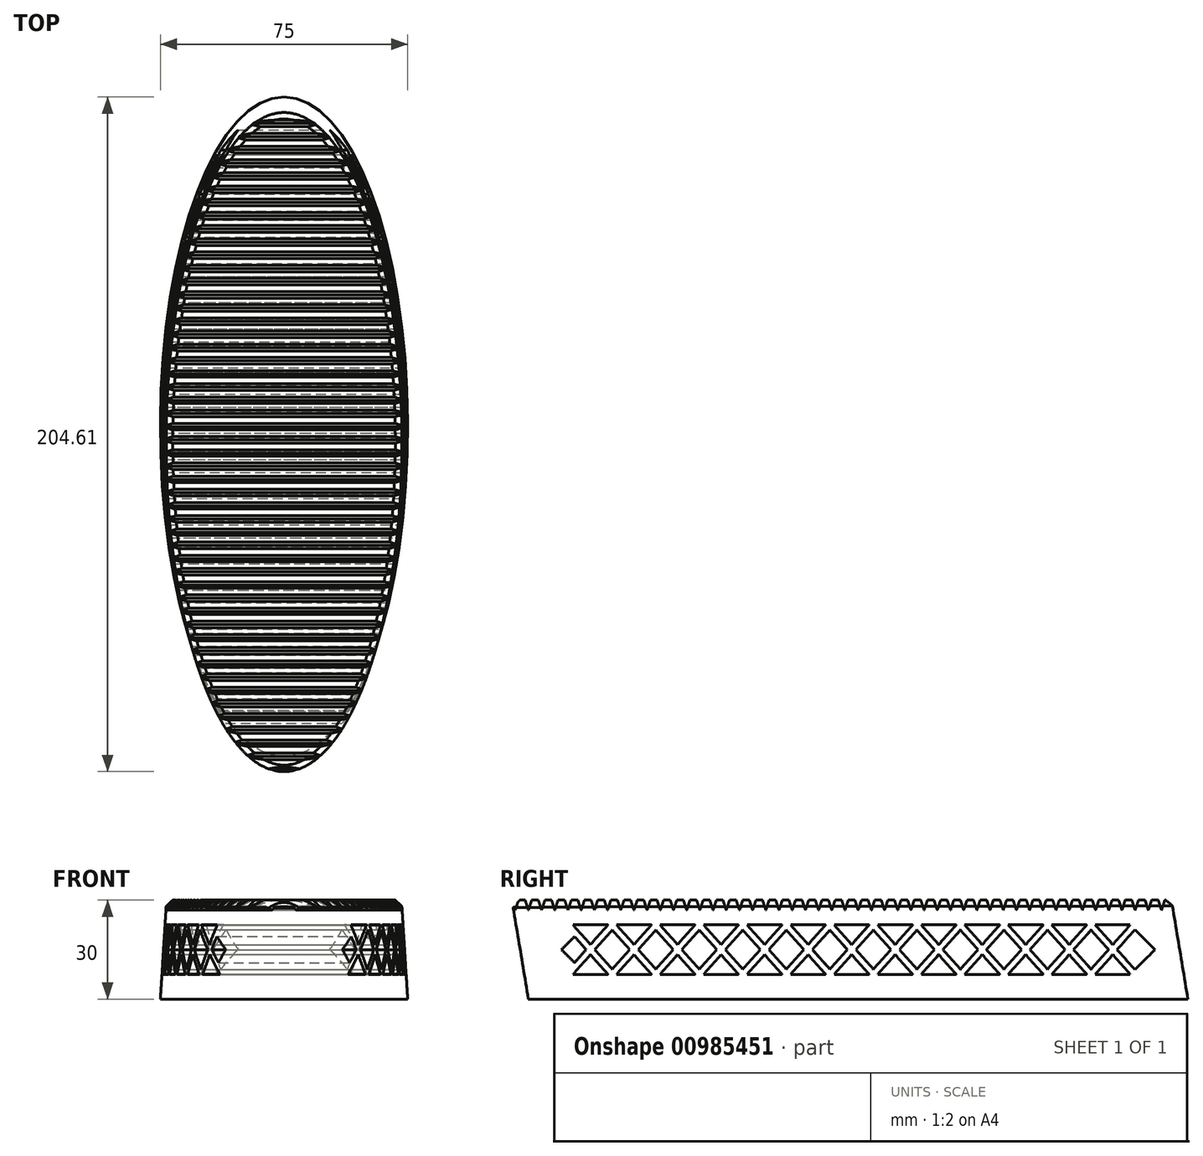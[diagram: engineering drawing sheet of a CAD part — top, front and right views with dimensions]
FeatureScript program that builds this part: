
annotation { "Feature Type Name" : "Feature", "Feature Type Description" : "" }
export const myFeature = defineFeature(function(context is Context, id is Id, definition is map)
    precondition{}
    {
        {
            assignVariable(context, id + "F0", {"name" : "Width", "anyValue" : 75});
        }
        {
            assignVariable(context, id + "F1", {"name" : "Thickness", "anyValue" : 30});
        }
        {
            var Q0;
            Q0=qCreatedBy(makeId("Top.planeOp"),FACE);
            var sketch = newSketch(context, id + "F2", { "sketchPlane" : qUnion([Q0])});
            skEllipse(sketch, "E0", {"center": v(0, 0) * mm, "majorRadius": 100 * mm, "minorRadius": 37.5 * mm, "majorAxis": v(0, 1)});
            skSolve(sketch);
        }
        {
            var Q0;
            Q0=makeQuery(id+"F2.imprint","IMPRINT",FACE,{"disambiguationData":[TD([[makeQuery(id+"F2.imprint","IMPRINT",EDGE,{"derivedFrom":sQuery(id+"F2.wireOp",EDGE,"E0")}),1.0]])]});
            cPlane(context, id + "F3", {"entities" : qUnion([Q0]), "cplaneType" : CPlaneType.OFFSET, "offset" : (getVariable(context, 'Thickness')) * mm, "width" : 150 * mm, "height" : 150 * mm});
        }
        {
            var Q0;
            Q0=qCreatedBy(id+"F3.planeOp",FACE);
            var sketch = newSketch(context, id + "F4", { "sketchPlane" : qUnion([Q0])});
            skEllipse(sketch, "E1", {"center": v(0, -5) * mm, "majorRadius": 100 * mm, "minorRadius": 35.63 * mm, "majorAxis": v(0, 1)});
            skEllipse(sketch, "E2.0", {"center": v(0, 0) * mm, "majorRadius": 100 * mm, "minorRadius": 37.5 * mm, "majorAxis": v(0, 1), "construction": true});
            skSolve(sketch);
        }
        {
            var Q0;
            Q0=makeQuery(id+"F2.imprint","IMPRINT",FACE,{"disambiguationData":[TD([[makeQuery(id+"F2.imprint","IMPRINT",EDGE,{"derivedFrom":sQuery(id+"F2.wireOp",EDGE,"E0")}),1.0]])]});
            var Q1;
            Q1=makeQuery(id+"F4.imprint","IMPRINT",FACE,{"disambiguationData":[TD([[makeQuery(id+"F4.imprint","IMPRINT",EDGE,{"derivedFrom":sQuery(id+"F4.wireOp",EDGE,"E1")}),1.0]])]});
            loft(context, id + "F5", {"sheetProfilesArray" : [{ "sheetProfileEntities" : qUnion([Q0]) }, { "sheetProfileEntities" : qUnion([Q1]) }]});
        }
        {
            var Q0;
            Q0=qCreatedBy(makeId("Right.planeOp"),FACE);
            var sketch = newSketch(context, id + "F6", { "sketchPlane" : qUnion([Q0])});
            skFitSpline(sketch, "E3.0", {"points": [v(95, 30) * mm, v(28.33, 30) * mm, v(-38.33, 30) * mm, v(-105, 30) * mm], "construction": true});
            skLineSegment(sketch, "E4", {"start": v(95, 30) * mm, "end": v(94, 33) * mm});
            skLineSegment(sketch, "E5", {"start": v(94, 33) * mm, "end": v(92, 27) * mm});
            skLineSegment(sketch, "E6", {"start": v(92, 27) * mm, "end": v(91, 30) * mm});
            skPoint(sketch, "E7", {"position": v(93, 30) * mm});
            skPoint(sketch, "E8", {"position": v(94, 30) * mm});
            skLineSegment(sketch, "E9.1.0.0", {"start": v(91, 30) * mm, "end": v(90, 33) * mm});
            skLineSegment(sketch, "E9.1.0.1", {"start": v(90, 33) * mm, "end": v(88, 27) * mm});
            skLineSegment(sketch, "E9.1.0.2", {"start": v(88, 27) * mm, "end": v(87, 30) * mm});
            skLineSegment(sketch, "E9.2.0.0", {"start": v(87, 30) * mm, "end": v(86, 33) * mm});
            skLineSegment(sketch, "E9.2.0.1", {"start": v(86, 33) * mm, "end": v(84, 27) * mm});
            skLineSegment(sketch, "E9.2.0.2", {"start": v(84, 27) * mm, "end": v(83, 30) * mm});
            skLineSegment(sketch, "E9.3.0.0", {"start": v(83, 30) * mm, "end": v(82, 33) * mm});
            skLineSegment(sketch, "E9.3.0.1", {"start": v(82, 33) * mm, "end": v(80, 27) * mm});
            skLineSegment(sketch, "E9.3.0.2", {"start": v(80, 27) * mm, "end": v(79, 30) * mm});
            skLineSegment(sketch, "E9.4.0.0", {"start": v(79, 30) * mm, "end": v(78, 33) * mm});
            skLineSegment(sketch, "E9.4.0.1", {"start": v(78, 33) * mm, "end": v(76, 27) * mm});
            skLineSegment(sketch, "E9.4.0.2", {"start": v(76, 27) * mm, "end": v(75, 30) * mm});
            skLineSegment(sketch, "E9.5.0.0", {"start": v(75, 30) * mm, "end": v(74, 33) * mm});
            skLineSegment(sketch, "E9.5.0.1", {"start": v(74, 33) * mm, "end": v(72, 27) * mm});
            skLineSegment(sketch, "E9.5.0.2", {"start": v(72, 27) * mm, "end": v(71, 30) * mm});
            skLineSegment(sketch, "E9.6.0.0", {"start": v(71, 30) * mm, "end": v(70, 33) * mm});
            skLineSegment(sketch, "E9.6.0.1", {"start": v(70, 33) * mm, "end": v(68, 27) * mm});
            skLineSegment(sketch, "E9.6.0.2", {"start": v(68, 27) * mm, "end": v(67, 30) * mm});
            skLineSegment(sketch, "E9.7.0.0", {"start": v(67, 30) * mm, "end": v(66, 33) * mm});
            skLineSegment(sketch, "E9.7.0.1", {"start": v(66, 33) * mm, "end": v(64, 27) * mm});
            skLineSegment(sketch, "E9.7.0.2", {"start": v(64, 27) * mm, "end": v(63, 30) * mm});
            skLineSegment(sketch, "E9.8.0.0", {"start": v(63, 30) * mm, "end": v(62, 33) * mm});
            skLineSegment(sketch, "E9.8.0.1", {"start": v(62, 33) * mm, "end": v(60, 27) * mm});
            skLineSegment(sketch, "E9.8.0.2", {"start": v(60, 27) * mm, "end": v(59, 30) * mm});
            skLineSegment(sketch, "E9.9.0.0", {"start": v(59, 30) * mm, "end": v(58, 33) * mm});
            skLineSegment(sketch, "E9.9.0.1", {"start": v(58, 33) * mm, "end": v(56, 27) * mm});
            skLineSegment(sketch, "E9.9.0.2", {"start": v(56, 27) * mm, "end": v(55, 30) * mm});
            skLineSegment(sketch, "E9.10.0.0", {"start": v(55, 30) * mm, "end": v(54, 33) * mm});
            skLineSegment(sketch, "E9.10.0.1", {"start": v(54, 33) * mm, "end": v(52, 27) * mm});
            skLineSegment(sketch, "E9.10.0.2", {"start": v(52, 27) * mm, "end": v(51, 30) * mm});
            skLineSegment(sketch, "E9.11.0.0", {"start": v(51, 30) * mm, "end": v(50, 33) * mm});
            skLineSegment(sketch, "E9.11.0.1", {"start": v(50, 33) * mm, "end": v(48, 27) * mm});
            skLineSegment(sketch, "E9.11.0.2", {"start": v(48, 27) * mm, "end": v(47, 30) * mm});
            skLineSegment(sketch, "E9.12.0.0", {"start": v(47, 30) * mm, "end": v(46, 33) * mm});
            skLineSegment(sketch, "E9.12.0.1", {"start": v(46, 33) * mm, "end": v(44, 27) * mm});
            skLineSegment(sketch, "E9.12.0.2", {"start": v(44, 27) * mm, "end": v(43, 30) * mm});
            skLineSegment(sketch, "E9.13.0.0", {"start": v(43, 30) * mm, "end": v(42, 33) * mm});
            skLineSegment(sketch, "E9.13.0.1", {"start": v(42, 33) * mm, "end": v(40, 27) * mm});
            skLineSegment(sketch, "E9.13.0.2", {"start": v(40, 27) * mm, "end": v(39, 30) * mm});
            skLineSegment(sketch, "E9.14.0.0", {"start": v(39, 30) * mm, "end": v(38, 33) * mm});
            skLineSegment(sketch, "E9.14.0.1", {"start": v(38, 33) * mm, "end": v(36, 27) * mm});
            skLineSegment(sketch, "E9.14.0.2", {"start": v(36, 27) * mm, "end": v(35, 30) * mm});
            skLineSegment(sketch, "E9.15.0.0", {"start": v(35, 30) * mm, "end": v(34, 33) * mm});
            skLineSegment(sketch, "E9.15.0.1", {"start": v(34, 33) * mm, "end": v(32, 27) * mm});
            skLineSegment(sketch, "E9.15.0.2", {"start": v(32, 27) * mm, "end": v(31, 30) * mm});
            skLineSegment(sketch, "E9.16.0.0", {"start": v(31, 30) * mm, "end": v(30, 33) * mm});
            skLineSegment(sketch, "E9.16.0.1", {"start": v(30, 33) * mm, "end": v(28, 27) * mm});
            skLineSegment(sketch, "E9.16.0.2", {"start": v(28, 27) * mm, "end": v(27, 30) * mm});
            skLineSegment(sketch, "E9.17.0.0", {"start": v(27, 30) * mm, "end": v(26, 33) * mm});
            skLineSegment(sketch, "E9.17.0.1", {"start": v(26, 33) * mm, "end": v(24, 27) * mm});
            skLineSegment(sketch, "E9.17.0.2", {"start": v(24, 27) * mm, "end": v(23, 30) * mm});
            skLineSegment(sketch, "E9.18.0.0", {"start": v(23, 30) * mm, "end": v(22, 33) * mm});
            skLineSegment(sketch, "E9.18.0.1", {"start": v(22, 33) * mm, "end": v(20, 27) * mm});
            skLineSegment(sketch, "E9.18.0.2", {"start": v(20, 27) * mm, "end": v(19, 30) * mm});
            skLineSegment(sketch, "E9.19.0.0", {"start": v(19, 30) * mm, "end": v(18, 33) * mm});
            skLineSegment(sketch, "E9.19.0.1", {"start": v(18, 33) * mm, "end": v(16, 27) * mm});
            skLineSegment(sketch, "E9.19.0.2", {"start": v(16, 27) * mm, "end": v(15, 30) * mm});
            skLineSegment(sketch, "E9.20.0.0", {"start": v(15, 30) * mm, "end": v(14, 33) * mm});
            skLineSegment(sketch, "E9.20.0.1", {"start": v(14, 33) * mm, "end": v(12, 27) * mm});
            skLineSegment(sketch, "E9.20.0.2", {"start": v(12, 27) * mm, "end": v(11, 30) * mm});
            skLineSegment(sketch, "E9.21.0.0", {"start": v(11, 30) * mm, "end": v(10, 33) * mm});
            skLineSegment(sketch, "E9.21.0.1", {"start": v(10, 33) * mm, "end": v(8, 27) * mm});
            skLineSegment(sketch, "E9.21.0.2", {"start": v(8, 27) * mm, "end": v(7, 30) * mm});
            skLineSegment(sketch, "E9.22.0.0", {"start": v(7, 30) * mm, "end": v(6, 33) * mm});
            skLineSegment(sketch, "E9.22.0.1", {"start": v(6, 33) * mm, "end": v(4, 27) * mm});
            skLineSegment(sketch, "E9.22.0.2", {"start": v(4, 27) * mm, "end": v(3, 30) * mm});
            skLineSegment(sketch, "E9.23.0.0", {"start": v(3, 30) * mm, "end": v(2, 33) * mm});
            skLineSegment(sketch, "E9.23.0.1", {"start": v(2, 33) * mm, "end": v(0, 27) * mm});
            skLineSegment(sketch, "E9.23.0.2", {"start": v(0, 27) * mm, "end": v(-1, 30) * mm});
            skLineSegment(sketch, "E9.24.0.0", {"start": v(-1, 30) * mm, "end": v(-2, 33) * mm});
            skLineSegment(sketch, "E9.24.0.1", {"start": v(-2, 33) * mm, "end": v(-4, 27) * mm});
            skLineSegment(sketch, "E9.24.0.2", {"start": v(-4, 27) * mm, "end": v(-5, 30) * mm});
            skLineSegment(sketch, "E9.25.0.0", {"start": v(-5, 30) * mm, "end": v(-6, 33) * mm});
            skLineSegment(sketch, "E9.25.0.1", {"start": v(-6, 33) * mm, "end": v(-8, 27) * mm});
            skLineSegment(sketch, "E9.25.0.2", {"start": v(-8, 27) * mm, "end": v(-9, 30) * mm});
            skLineSegment(sketch, "E9.26.0.0", {"start": v(-9, 30) * mm, "end": v(-10, 33) * mm});
            skLineSegment(sketch, "E9.26.0.1", {"start": v(-10, 33) * mm, "end": v(-12, 27) * mm});
            skLineSegment(sketch, "E9.26.0.2", {"start": v(-12, 27) * mm, "end": v(-13, 30) * mm});
            skLineSegment(sketch, "E9.27.0.0", {"start": v(-13, 30) * mm, "end": v(-14, 33) * mm});
            skLineSegment(sketch, "E9.27.0.1", {"start": v(-14, 33) * mm, "end": v(-16, 27) * mm});
            skLineSegment(sketch, "E9.27.0.2", {"start": v(-16, 27) * mm, "end": v(-17, 30) * mm});
            skLineSegment(sketch, "E9.28.0.0", {"start": v(-17, 30) * mm, "end": v(-18, 33) * mm});
            skLineSegment(sketch, "E9.28.0.1", {"start": v(-18, 33) * mm, "end": v(-20, 27) * mm});
            skLineSegment(sketch, "E9.28.0.2", {"start": v(-20, 27) * mm, "end": v(-21, 30) * mm});
            skLineSegment(sketch, "E9.29.0.0", {"start": v(-21, 30) * mm, "end": v(-22, 33) * mm});
            skLineSegment(sketch, "E9.29.0.1", {"start": v(-22, 33) * mm, "end": v(-24, 27) * mm});
            skLineSegment(sketch, "E9.29.0.2", {"start": v(-24, 27) * mm, "end": v(-25, 30) * mm});
            skLineSegment(sketch, "E9.30.0.0", {"start": v(-25, 30) * mm, "end": v(-26, 33) * mm});
            skLineSegment(sketch, "E9.30.0.1", {"start": v(-26, 33) * mm, "end": v(-28, 27) * mm});
            skLineSegment(sketch, "E9.30.0.2", {"start": v(-28, 27) * mm, "end": v(-29, 30) * mm});
            skLineSegment(sketch, "E9.31.0.0", {"start": v(-29, 30) * mm, "end": v(-30, 33) * mm});
            skLineSegment(sketch, "E9.31.0.1", {"start": v(-30, 33) * mm, "end": v(-32, 27) * mm});
            skLineSegment(sketch, "E9.31.0.2", {"start": v(-32, 27) * mm, "end": v(-33, 30) * mm});
            skLineSegment(sketch, "E9.32.0.0", {"start": v(-33, 30) * mm, "end": v(-34, 33) * mm});
            skLineSegment(sketch, "E9.32.0.1", {"start": v(-34, 33) * mm, "end": v(-36, 27) * mm});
            skLineSegment(sketch, "E9.32.0.2", {"start": v(-36, 27) * mm, "end": v(-37, 30) * mm});
            skLineSegment(sketch, "E9.33.0.0", {"start": v(-37, 30) * mm, "end": v(-38, 33) * mm});
            skLineSegment(sketch, "E9.33.0.1", {"start": v(-38, 33) * mm, "end": v(-40, 27) * mm});
            skLineSegment(sketch, "E9.33.0.2", {"start": v(-40, 27) * mm, "end": v(-41, 30) * mm});
            skLineSegment(sketch, "E9.34.0.0", {"start": v(-41, 30) * mm, "end": v(-42, 33) * mm});
            skLineSegment(sketch, "E9.34.0.1", {"start": v(-42, 33) * mm, "end": v(-44, 27) * mm});
            skLineSegment(sketch, "E9.34.0.2", {"start": v(-44, 27) * mm, "end": v(-45, 30) * mm});
            skLineSegment(sketch, "E9.35.0.0", {"start": v(-45, 30) * mm, "end": v(-46, 33) * mm});
            skLineSegment(sketch, "E9.35.0.1", {"start": v(-46, 33) * mm, "end": v(-48, 27) * mm});
            skLineSegment(sketch, "E9.35.0.2", {"start": v(-48, 27) * mm, "end": v(-49, 30) * mm});
            skLineSegment(sketch, "E9.36.0.0", {"start": v(-49, 30) * mm, "end": v(-50, 33) * mm});
            skLineSegment(sketch, "E9.36.0.1", {"start": v(-50, 33) * mm, "end": v(-52, 27) * mm});
            skLineSegment(sketch, "E9.36.0.2", {"start": v(-52, 27) * mm, "end": v(-53, 30) * mm});
            skLineSegment(sketch, "E9.37.0.0", {"start": v(-53, 30) * mm, "end": v(-54, 33) * mm});
            skLineSegment(sketch, "E9.37.0.1", {"start": v(-54, 33) * mm, "end": v(-56, 27) * mm});
            skLineSegment(sketch, "E9.37.0.2", {"start": v(-56, 27) * mm, "end": v(-57, 30) * mm});
            skLineSegment(sketch, "E9.38.0.0", {"start": v(-57, 30) * mm, "end": v(-58, 33) * mm});
            skLineSegment(sketch, "E9.38.0.1", {"start": v(-58, 33) * mm, "end": v(-60, 27) * mm});
            skLineSegment(sketch, "E9.38.0.2", {"start": v(-60, 27) * mm, "end": v(-61, 30) * mm});
            skLineSegment(sketch, "E9.39.0.0", {"start": v(-61, 30) * mm, "end": v(-62, 33) * mm});
            skLineSegment(sketch, "E9.39.0.1", {"start": v(-62, 33) * mm, "end": v(-64, 27) * mm});
            skLineSegment(sketch, "E9.39.0.2", {"start": v(-64, 27) * mm, "end": v(-65, 30) * mm});
            skLineSegment(sketch, "E9.40.0.0", {"start": v(-65, 30) * mm, "end": v(-66, 33) * mm});
            skLineSegment(sketch, "E9.40.0.1", {"start": v(-66, 33) * mm, "end": v(-68, 27) * mm});
            skLineSegment(sketch, "E9.40.0.2", {"start": v(-68, 27) * mm, "end": v(-69, 30) * mm});
            skLineSegment(sketch, "E9.41.0.0", {"start": v(-69, 30) * mm, "end": v(-70, 33) * mm});
            skLineSegment(sketch, "E9.41.0.1", {"start": v(-70, 33) * mm, "end": v(-72, 27) * mm});
            skLineSegment(sketch, "E9.41.0.2", {"start": v(-72, 27) * mm, "end": v(-73, 30) * mm});
            skLineSegment(sketch, "E9.42.0.0", {"start": v(-73, 30) * mm, "end": v(-74, 33) * mm});
            skLineSegment(sketch, "E9.42.0.1", {"start": v(-74, 33) * mm, "end": v(-76, 27) * mm});
            skLineSegment(sketch, "E9.42.0.2", {"start": v(-76, 27) * mm, "end": v(-77, 30) * mm});
            skLineSegment(sketch, "E9.43.0.0", {"start": v(-77, 30) * mm, "end": v(-78, 33) * mm});
            skLineSegment(sketch, "E9.43.0.1", {"start": v(-78, 33) * mm, "end": v(-80, 27) * mm});
            skLineSegment(sketch, "E9.43.0.2", {"start": v(-80, 27) * mm, "end": v(-81, 30) * mm});
            skLineSegment(sketch, "E9.44.0.0", {"start": v(-81, 30) * mm, "end": v(-82, 33) * mm});
            skLineSegment(sketch, "E9.44.0.1", {"start": v(-82, 33) * mm, "end": v(-84, 27) * mm});
            skLineSegment(sketch, "E9.44.0.2", {"start": v(-84, 27) * mm, "end": v(-85, 30) * mm});
            skLineSegment(sketch, "E9.45.0.0", {"start": v(-85, 30) * mm, "end": v(-86, 33) * mm});
            skLineSegment(sketch, "E9.45.0.1", {"start": v(-86, 33) * mm, "end": v(-88, 27) * mm});
            skLineSegment(sketch, "E9.45.0.2", {"start": v(-88, 27) * mm, "end": v(-89, 30) * mm});
            skLineSegment(sketch, "E9.46.0.0", {"start": v(-89, 30) * mm, "end": v(-90, 33) * mm});
            skLineSegment(sketch, "E9.46.0.1", {"start": v(-90, 33) * mm, "end": v(-92, 27) * mm});
            skLineSegment(sketch, "E9.46.0.2", {"start": v(-92, 27) * mm, "end": v(-93, 30) * mm});
            skLineSegment(sketch, "E9.47.0.0", {"start": v(-93, 30) * mm, "end": v(-94, 33) * mm});
            skLineSegment(sketch, "E9.47.0.1", {"start": v(-94, 33) * mm, "end": v(-96, 27) * mm});
            skLineSegment(sketch, "E9.47.0.2", {"start": v(-96, 27) * mm, "end": v(-97, 30) * mm});
            skLineSegment(sketch, "E9.48.0.0", {"start": v(-97, 30) * mm, "end": v(-98, 33) * mm});
            skLineSegment(sketch, "E9.48.0.1", {"start": v(-98, 33) * mm, "end": v(-100, 27) * mm});
            skLineSegment(sketch, "E9.48.0.2", {"start": v(-100, 27) * mm, "end": v(-101, 30) * mm});
            skLineSegment(sketch, "E9.49.0.0", {"start": v(-101, 30) * mm, "end": v(-102, 33) * mm});
            skLineSegment(sketch, "E9.49.0.1", {"start": v(-102, 33) * mm, "end": v(-104, 27) * mm});
            skLineSegment(sketch, "E9.49.0.2", {"start": v(-104, 27) * mm, "end": v(-105, 30) * mm});
            skLineSegment(sketch, "E9.direction1", {"start": v(95, 30) * mm, "end": v(91, 30) * mm, "construction": true});
            skLineSegment(sketch, "E10", {"start": v(94, 33) * mm, "end": v(-105, 33) * mm});
            skLineSegment(sketch, "E11", {"start": v(-105, 33) * mm, "end": v(-105, 30) * mm});
            skSolve(sketch);
        }
        {
            var Q0;
            Q0=makeQuery(id+"F5.opLoft","MID_CAP_EDGE",EDGE,{"disambiguationData":[OSD([sQuery(id+"F4.wireOp",EDGE,"E1")])],"capPos":1.0});
            chamfer(context, id + "F7", {"entities" : qUnion([Q0]), "width" : 2 * mm, "tangentPropagation" : true});
        }
        {
            var Q0;
            Q0 = qSketchRegion(id + "F6", true);
            extrude(context, id + "F8", {"entities" : qUnion([Q0]), "operationType" : NewBodyOperationType.REMOVE, "endBound" : BoundingType.SYMMETRIC, "oppositeDirection" : true, "depth" : (getVariable(context, 'Width')) * mm, "offsetDistance" : 25 * mm});
        }
        {
            var Q0;
            Q0=qCreatedBy(makeId("Right.planeOp"),FACE);
            var sketch = newSketch(context, id + "F9", { "sketchPlane" : qUnion([Q0])});
            skLineSegment(sketch, "E12.bottom", {"start": v(-90, 22.5) * mm, "end": v(90, 22.5) * mm});
            skLineSegment(sketch, "E12.top", {"start": v(-90, 7.5) * mm, "end": v(90, 7.5) * mm});
            skLineSegment(sketch, "E12.left", {"start": v(-90, 22.5) * mm, "end": v(-90, 7.5) * mm});
            skLineSegment(sketch, "E12.right", {"start": v(90, 22.5) * mm, "end": v(90, 7.5) * mm});
            skPoint(sketch, "E12.middle", {"position": v(0, 15) * mm});
            skLineSegment(sketch, "E13", {"start": v(90, 15) * mm, "end": v(82.5, 22.5) * mm});
            skLineSegment(sketch, "E14.MirrorCS", {"start": v(-90, 15) * mm, "end": v(-82.5, 22.5) * mm});
            skLineSegment(sketch, "E15", {"start": v(90, 15) * mm, "end": v(-90, 15) * mm, "construction": true});
            skLineSegment(sketch, "E16.MirrorCS", {"start": v(90, 15) * mm, "end": v(82.5, 7.5) * mm});
            skLineSegment(sketch, "E17.MirrorCS", {"start": v(-90, 15) * mm, "end": v(-82.5, 7.5) * mm});
            skLineSegment(sketch, "E18", {"start": v(82.5, 22.5) * mm, "end": v(69.27, 7.5) * mm});
            skLineSegment(sketch, "E19", {"start": v(83.92, 21.08) * mm, "end": v(71.94, 7.5) * mm});
            skLineSegment(sketch, "E20.MirrorCS", {"start": v(83.92, 8.92) * mm, "end": v(71.94, 22.5) * mm});
            skLineSegment(sketch, "E21.MirrorCS", {"start": v(82.5, 7.5) * mm, "end": v(69.27, 22.5) * mm});
            skLineSegment(sketch, "E22.1.0.0", {"start": v(70.72, 21.08) * mm, "end": v(58.74, 7.5) * mm});
            skLineSegment(sketch, "E22.1.0.1", {"start": v(69.3, 22.5) * mm, "end": v(56.07, 7.5) * mm});
            skLineSegment(sketch, "E22.1.0.2", {"start": v(70.72, 8.92) * mm, "end": v(58.74, 22.5) * mm});
            skLineSegment(sketch, "E22.1.0.3", {"start": v(69.3, 7.5) * mm, "end": v(56.07, 22.5) * mm});
            skLineSegment(sketch, "E22.1.0.4", {"start": v(76.8, 15) * mm, "end": v(-103.2, 15) * mm, "construction": true});
            skLineSegment(sketch, "E22.2.0.0", {"start": v(57.52, 21.08) * mm, "end": v(45.54, 7.5) * mm});
            skLineSegment(sketch, "E22.2.0.1", {"start": v(56.1, 22.5) * mm, "end": v(42.87, 7.5) * mm});
            skLineSegment(sketch, "E22.2.0.2", {"start": v(57.52, 8.92) * mm, "end": v(45.54, 22.5) * mm});
            skLineSegment(sketch, "E22.2.0.3", {"start": v(56.1, 7.5) * mm, "end": v(42.87, 22.5) * mm});
            skLineSegment(sketch, "E22.2.0.4", {"start": v(63.6, 15) * mm, "end": v(-116.4, 15) * mm, "construction": true});
            skLineSegment(sketch, "E22.3.0.0", {"start": v(44.32, 21.08) * mm, "end": v(32.34, 7.5) * mm});
            skLineSegment(sketch, "E22.3.0.1", {"start": v(42.9, 22.5) * mm, "end": v(29.67, 7.5) * mm});
            skLineSegment(sketch, "E22.3.0.2", {"start": v(44.32, 8.92) * mm, "end": v(32.34, 22.5) * mm});
            skLineSegment(sketch, "E22.3.0.3", {"start": v(42.9, 7.5) * mm, "end": v(29.67, 22.5) * mm});
            skLineSegment(sketch, "E22.3.0.4", {"start": v(50.4, 15) * mm, "end": v(-129.6, 15) * mm, "construction": true});
            skLineSegment(sketch, "E22.4.0.0", {"start": v(31.12, 21.08) * mm, "end": v(19.14, 7.5) * mm});
            skLineSegment(sketch, "E22.4.0.1", {"start": v(29.7, 22.5) * mm, "end": v(16.47, 7.5) * mm});
            skLineSegment(sketch, "E22.4.0.2", {"start": v(31.12, 8.92) * mm, "end": v(19.14, 22.5) * mm});
            skLineSegment(sketch, "E22.4.0.3", {"start": v(29.7, 7.5) * mm, "end": v(16.47, 22.5) * mm});
            skLineSegment(sketch, "E22.4.0.4", {"start": v(37.2, 15) * mm, "end": v(-142.8, 15) * mm, "construction": true});
            skLineSegment(sketch, "E22.5.0.0", {"start": v(17.92, 21.08) * mm, "end": v(5.94, 7.5) * mm});
            skLineSegment(sketch, "E22.5.0.1", {"start": v(16.5, 22.5) * mm, "end": v(3.27, 7.5) * mm});
            skLineSegment(sketch, "E22.5.0.2", {"start": v(17.92, 8.92) * mm, "end": v(5.94, 22.5) * mm});
            skLineSegment(sketch, "E22.5.0.3", {"start": v(16.5, 7.5) * mm, "end": v(3.27, 22.5) * mm});
            skLineSegment(sketch, "E22.5.0.4", {"start": v(24, 15) * mm, "end": v(-156, 15) * mm, "construction": true});
            skLineSegment(sketch, "E22.6.0.0", {"start": v(4.72, 21.08) * mm, "end": v(-7.26, 7.5) * mm});
            skLineSegment(sketch, "E22.6.0.1", {"start": v(3.3, 22.5) * mm, "end": v(-9.93, 7.5) * mm});
            skLineSegment(sketch, "E22.6.0.2", {"start": v(4.72, 8.92) * mm, "end": v(-7.26, 22.5) * mm});
            skLineSegment(sketch, "E22.6.0.3", {"start": v(3.3, 7.5) * mm, "end": v(-9.93, 22.5) * mm});
            skLineSegment(sketch, "E22.6.0.4", {"start": v(10.8, 15) * mm, "end": v(-169.2, 15) * mm, "construction": true});
            skLineSegment(sketch, "E22.7.0.0", {"start": v(-8.48, 21.08) * mm, "end": v(-20.46, 7.5) * mm});
            skLineSegment(sketch, "E22.7.0.1", {"start": v(-9.9, 22.5) * mm, "end": v(-23.13, 7.5) * mm});
            skLineSegment(sketch, "E22.7.0.2", {"start": v(-8.48, 8.92) * mm, "end": v(-20.46, 22.5) * mm});
            skLineSegment(sketch, "E22.7.0.3", {"start": v(-9.9, 7.5) * mm, "end": v(-23.13, 22.5) * mm});
            skLineSegment(sketch, "E22.7.0.4", {"start": v(-2.4, 15) * mm, "end": v(-182.4, 15) * mm, "construction": true});
            skLineSegment(sketch, "E22.8.0.0", {"start": v(-21.68, 21.08) * mm, "end": v(-33.66, 7.5) * mm});
            skLineSegment(sketch, "E22.8.0.1", {"start": v(-23.1, 22.5) * mm, "end": v(-36.33, 7.5) * mm});
            skLineSegment(sketch, "E22.8.0.2", {"start": v(-21.68, 8.92) * mm, "end": v(-33.66, 22.5) * mm});
            skLineSegment(sketch, "E22.8.0.3", {"start": v(-23.1, 7.5) * mm, "end": v(-36.33, 22.5) * mm});
            skLineSegment(sketch, "E22.8.0.4", {"start": v(-15.6, 15) * mm, "end": v(-195.6, 15) * mm, "construction": true});
            skLineSegment(sketch, "E22.9.0.0", {"start": v(-34.88, 21.08) * mm, "end": v(-46.86, 7.5) * mm});
            skLineSegment(sketch, "E22.9.0.1", {"start": v(-36.3, 22.5) * mm, "end": v(-49.53, 7.5) * mm});
            skLineSegment(sketch, "E22.9.0.2", {"start": v(-34.88, 8.92) * mm, "end": v(-46.86, 22.5) * mm});
            skLineSegment(sketch, "E22.9.0.3", {"start": v(-36.3, 7.5) * mm, "end": v(-49.53, 22.5) * mm});
            skLineSegment(sketch, "E22.9.0.4", {"start": v(-28.8, 15) * mm, "end": v(-208.8, 15) * mm, "construction": true});
            skLineSegment(sketch, "E22.10.0.0", {"start": v(-48.08, 21.08) * mm, "end": v(-60.06, 7.5) * mm});
            skLineSegment(sketch, "E22.10.0.1", {"start": v(-49.5, 22.5) * mm, "end": v(-62.73, 7.5) * mm});
            skLineSegment(sketch, "E22.10.0.2", {"start": v(-48.08, 8.92) * mm, "end": v(-60.06, 22.5) * mm});
            skLineSegment(sketch, "E22.10.0.3", {"start": v(-49.5, 7.5) * mm, "end": v(-62.73, 22.5) * mm});
            skLineSegment(sketch, "E22.10.0.4", {"start": v(-42, 15) * mm, "end": v(-222, 15) * mm, "construction": true});
            skLineSegment(sketch, "E22.11.0.0", {"start": v(-61.28, 21.08) * mm, "end": v(-73.26, 7.5) * mm});
            skLineSegment(sketch, "E22.11.0.1", {"start": v(-62.7, 22.5) * mm, "end": v(-75.93, 7.5) * mm});
            skLineSegment(sketch, "E22.11.0.2", {"start": v(-61.28, 8.92) * mm, "end": v(-73.26, 22.5) * mm});
            skLineSegment(sketch, "E22.11.0.3", {"start": v(-62.7, 7.5) * mm, "end": v(-75.93, 22.5) * mm});
            skLineSegment(sketch, "E22.11.0.4", {"start": v(-55.2, 15) * mm, "end": v(-235.2, 15) * mm, "construction": true});
            skLineSegment(sketch, "E22.12.0.0", {"start": v(-74.48, 21.08) * mm, "end": v(-86.46, 7.5) * mm});
            skLineSegment(sketch, "E22.12.0.1", {"start": v(-75.9, 22.5) * mm, "end": v(-89.13, 7.5) * mm});
            skLineSegment(sketch, "E22.12.0.2", {"start": v(-74.48, 8.92) * mm, "end": v(-86.46, 22.5) * mm});
            skLineSegment(sketch, "E22.12.0.3", {"start": v(-75.9, 7.5) * mm, "end": v(-89.13, 22.5) * mm});
            skLineSegment(sketch, "E22.12.0.4", {"start": v(-68.4, 15) * mm, "end": v(-248.4, 15) * mm, "construction": true});
            skLineSegment(sketch, "E22.direction1", {"start": v(71.94, 7.5) * mm, "end": v(58.74, 7.5) * mm, "construction": true});
            skSolve(sketch);
        }
        {
            var Q0;
            {var subQ0=sQuery(id+"F9.wireOp",EDGE,"E22.1.0.2");var subQ1=sQuery(id+"F9.wireOp",EDGE,"E18");var subQ2=makeQuery(id+"F9.imprint","INTERSECT",VERTEX,{"derivedFrom":[subQ1,subQ0]});Q0=makeQuery(id+"F9.imprint","IMPRINT",FACE,{"disambiguationData":[TD([[makeQuery(id+"F9.imprint","IMPRINT",EDGE,{"disambiguationData":[TD([[subQ2,1.0]])],"derivedFrom":subQ1}),-1.0]])]});}
            var Q1;
            {var subQ0=sQuery(id+"F9.wireOp",EDGE,"E22.2.0.2");var subQ1=sQuery(id+"F9.wireOp",EDGE,"E22.1.0.1");var subQ2=makeQuery(id+"F9.imprint","INTERSECT",VERTEX,{"derivedFrom":[subQ1,subQ0]});Q1=makeQuery(id+"F9.imprint","IMPRINT",FACE,{"disambiguationData":[TD([[makeQuery(id+"F9.imprint","IMPRINT",EDGE,{"disambiguationData":[TD([[subQ2,1.0]])],"derivedFrom":subQ1}),-1.0]])]});}
            var Q2;
            {var subQ0=sQuery(id+"F9.wireOp",EDGE,"E22.4.0.2");var subQ1=sQuery(id+"F9.wireOp",EDGE,"E22.3.0.1");var subQ2=makeQuery(id+"F9.imprint","INTERSECT",VERTEX,{"derivedFrom":[subQ1,subQ0]});Q2=makeQuery(id+"F9.imprint","IMPRINT",FACE,{"disambiguationData":[TD([[makeQuery(id+"F9.imprint","IMPRINT",EDGE,{"disambiguationData":[TD([[subQ2,1.0]])],"derivedFrom":subQ1}),-1.0]])]});}
            var Q3;
            {var subQ0=sQuery(id+"F9.wireOp",EDGE,"E22.5.0.2");var subQ1=sQuery(id+"F9.wireOp",EDGE,"E22.4.0.1");var subQ2=makeQuery(id+"F9.imprint","INTERSECT",VERTEX,{"derivedFrom":[subQ1,subQ0]});Q3=makeQuery(id+"F9.imprint","IMPRINT",FACE,{"disambiguationData":[TD([[makeQuery(id+"F9.imprint","IMPRINT",EDGE,{"disambiguationData":[TD([[subQ2,1.0]])],"derivedFrom":subQ1}),-1.0]])]});}
            var Q4;
            {var subQ0=sQuery(id+"F9.wireOp",EDGE,"E22.3.0.2");var subQ1=sQuery(id+"F9.wireOp",EDGE,"E22.2.0.1");var subQ2=makeQuery(id+"F9.imprint","INTERSECT",VERTEX,{"derivedFrom":[subQ1,subQ0]});Q4=makeQuery(id+"F9.imprint","IMPRINT",FACE,{"disambiguationData":[TD([[makeQuery(id+"F9.imprint","IMPRINT",EDGE,{"disambiguationData":[TD([[subQ2,1.0]])],"derivedFrom":subQ1}),-1.0]])]});}
            var Q5;
            {var subQ0=sQuery(id+"F9.wireOp",EDGE,"E22.6.0.2");var subQ1=sQuery(id+"F9.wireOp",EDGE,"E22.5.0.1");var subQ2=makeQuery(id+"F9.imprint","INTERSECT",VERTEX,{"derivedFrom":[subQ1,subQ0]});Q5=makeQuery(id+"F9.imprint","IMPRINT",FACE,{"disambiguationData":[TD([[makeQuery(id+"F9.imprint","IMPRINT",EDGE,{"disambiguationData":[TD([[subQ2,1.0]])],"derivedFrom":subQ1}),-1.0]])]});}
            var Q6;
            {var subQ0=sQuery(id+"F9.wireOp",EDGE,"E22.7.0.2");var subQ1=sQuery(id+"F9.wireOp",EDGE,"E22.6.0.1");var subQ2=makeQuery(id+"F9.imprint","INTERSECT",VERTEX,{"derivedFrom":[subQ1,subQ0]});Q6=makeQuery(id+"F9.imprint","IMPRINT",FACE,{"disambiguationData":[TD([[makeQuery(id+"F9.imprint","IMPRINT",EDGE,{"disambiguationData":[TD([[subQ2,1.0]])],"derivedFrom":subQ1}),-1.0]])]});}
            var Q7;
            {var subQ0=sQuery(id+"F9.wireOp",EDGE,"E22.8.0.2");var subQ1=sQuery(id+"F9.wireOp",EDGE,"E22.7.0.1");var subQ2=makeQuery(id+"F9.imprint","INTERSECT",VERTEX,{"derivedFrom":[subQ1,subQ0]});Q7=makeQuery(id+"F9.imprint","IMPRINT",FACE,{"disambiguationData":[TD([[makeQuery(id+"F9.imprint","IMPRINT",EDGE,{"disambiguationData":[TD([[subQ2,1.0]])],"derivedFrom":subQ1}),-1.0]])]});}
            var Q8;
            {var subQ0=sQuery(id+"F9.wireOp",EDGE,"E22.9.0.2");var subQ1=sQuery(id+"F9.wireOp",EDGE,"E22.8.0.1");var subQ2=makeQuery(id+"F9.imprint","INTERSECT",VERTEX,{"derivedFrom":[subQ1,subQ0]});Q8=makeQuery(id+"F9.imprint","IMPRINT",FACE,{"disambiguationData":[TD([[makeQuery(id+"F9.imprint","IMPRINT",EDGE,{"disambiguationData":[TD([[subQ2,1.0]])],"derivedFrom":subQ1}),-1.0]])]});}
            var Q9;
            {var subQ0=sQuery(id+"F9.wireOp",EDGE,"E22.10.0.2");var subQ1=sQuery(id+"F9.wireOp",EDGE,"E22.9.0.1");var subQ2=makeQuery(id+"F9.imprint","INTERSECT",VERTEX,{"derivedFrom":[subQ1,subQ0]});Q9=makeQuery(id+"F9.imprint","IMPRINT",FACE,{"disambiguationData":[TD([[makeQuery(id+"F9.imprint","IMPRINT",EDGE,{"disambiguationData":[TD([[subQ2,1.0]])],"derivedFrom":subQ1}),-1.0]])]});}
            var Q10;
            {var subQ0=sQuery(id+"F9.wireOp",EDGE,"E22.11.0.2");var subQ1=sQuery(id+"F9.wireOp",EDGE,"E22.10.0.1");var subQ2=makeQuery(id+"F9.imprint","INTERSECT",VERTEX,{"derivedFrom":[subQ1,subQ0]});Q10=makeQuery(id+"F9.imprint","IMPRINT",FACE,{"disambiguationData":[TD([[makeQuery(id+"F9.imprint","IMPRINT",EDGE,{"disambiguationData":[TD([[subQ2,1.0]])],"derivedFrom":subQ1}),-1.0]])]});}
            var Q11;
            {var subQ0=sQuery(id+"F9.wireOp",EDGE,"E22.12.0.2");var subQ1=sQuery(id+"F9.wireOp",EDGE,"E22.11.0.1");var subQ2=makeQuery(id+"F9.imprint","INTERSECT",VERTEX,{"derivedFrom":[subQ1,subQ0]});Q11=makeQuery(id+"F9.imprint","IMPRINT",FACE,{"disambiguationData":[TD([[makeQuery(id+"F9.imprint","IMPRINT",EDGE,{"disambiguationData":[TD([[subQ2,1.0]])],"derivedFrom":subQ1}),-1.0]])]});}
            var Q12;
            {var subQ0=sQuery(id+"F9.wireOp",EDGE,"E17.MirrorCS");var subQ5=sQuery(id+"F9.wireOp",EDGE,"E22.12.0.1");var subQ6=makeQuery(id+"F9.imprint","INTERSECT",VERTEX,{"derivedFrom":[subQ0,subQ5]});Q12=makeQuery(id+"F9.imprint","IMPRINT",FACE,{"disambiguationData":[TD([[makeQuery(id+"F9.imprint","IMPRINT",EDGE,{"disambiguationData":[TD([[subQ6,1.0]])],"derivedFrom":subQ5}),-1.0]])]});}
            var Q13;
            {var subQ1=sQuery(id+"F9.wireOp",EDGE,"E17.MirrorCS");var subQ6=sQuery(id+"F9.wireOp",EDGE,"E12.top");var subQ9=makeQuery(id+"F9.imprint","INTERSECT",VERTEX,{"derivedFrom":[subQ6,subQ1]});Q13=makeQuery(id+"F9.imprint","IMPRINT",FACE,{"disambiguationData":[TD([[makeQuery(id+"F9.imprint","IMPRINT",EDGE,{"disambiguationData":[TD([[subQ9,-1.0]])],"derivedFrom":subQ6}),1.0]])]});}
            var Q14;
            {var subQ0=sQuery(id+"F9.wireOp",EDGE,"E17.MirrorCS");var subQ1=sQuery(id+"F9.wireOp",EDGE,"E12.top");var subQ2=makeQuery(id+"F9.imprint","INTERSECT",VERTEX,{"derivedFrom":[subQ1,subQ0]});Q14=makeQuery(id+"F9.imprint","IMPRINT",FACE,{"disambiguationData":[TD([[makeQuery(id+"F9.imprint","IMPRINT",EDGE,{"disambiguationData":[TD([[subQ2,1.0]])],"derivedFrom":subQ1}),1.0]])]});}
            var Q15;
            {var subQ1=sQuery(id+"F9.wireOp",EDGE,"E12.bottom");var subQ7=sQuery(id+"F9.wireOp",EDGE,"E14.MirrorCS");var subQ8=makeQuery(id+"F9.imprint","INTERSECT",VERTEX,{"derivedFrom":[subQ1,subQ7]});Q15=makeQuery(id+"F9.imprint","IMPRINT",FACE,{"disambiguationData":[TD([[makeQuery(id+"F9.imprint","IMPRINT",EDGE,{"disambiguationData":[TD([[subQ8,-1.0]])],"derivedFrom":subQ1}),-1.0]])]});}
            var Q16;
            {var subQ0=sQuery(id+"F9.wireOp",EDGE,"E14.MirrorCS");var subQ1=sQuery(id+"F9.wireOp",EDGE,"E12.bottom");var subQ2=makeQuery(id+"F9.imprint","INTERSECT",VERTEX,{"derivedFrom":[subQ1,subQ0]});Q16=makeQuery(id+"F9.imprint","IMPRINT",FACE,{"disambiguationData":[TD([[makeQuery(id+"F9.imprint","IMPRINT",EDGE,{"disambiguationData":[TD([[subQ2,1.0]])],"derivedFrom":subQ1}),-1.0]])]});}
            var Q17;
            {var subQ0=sQuery(id+"F9.wireOp",EDGE,"E22.10.0.3");var subQ1=sQuery(id+"F9.wireOp",EDGE,"E12.bottom");var subQ2=makeQuery(id+"F9.imprint","INTERSECT",VERTEX,{"derivedFrom":[subQ1,subQ0]});Q17=makeQuery(id+"F9.imprint","IMPRINT",FACE,{"disambiguationData":[TD([[makeQuery(id+"F9.imprint","IMPRINT",EDGE,{"disambiguationData":[TD([[subQ2,1.0]])],"derivedFrom":subQ1}),-1.0]])]});}
            var Q18;
            {var subQ0=sQuery(id+"F9.wireOp",EDGE,"E22.10.0.1");var subQ1=sQuery(id+"F9.wireOp",EDGE,"E12.top");var subQ2=makeQuery(id+"F9.imprint","INTERSECT",VERTEX,{"derivedFrom":[subQ1,subQ0]});Q18=makeQuery(id+"F9.imprint","IMPRINT",FACE,{"disambiguationData":[TD([[makeQuery(id+"F9.imprint","IMPRINT",EDGE,{"disambiguationData":[TD([[subQ2,1.0]])],"derivedFrom":subQ1}),1.0]])]});}
            var Q19;
            {var subQ0=sQuery(id+"F9.wireOp",EDGE,"E22.9.0.1");var subQ1=sQuery(id+"F9.wireOp",EDGE,"E12.top");var subQ2=makeQuery(id+"F9.imprint","INTERSECT",VERTEX,{"derivedFrom":[subQ1,subQ0]});Q19=makeQuery(id+"F9.imprint","IMPRINT",FACE,{"disambiguationData":[TD([[makeQuery(id+"F9.imprint","IMPRINT",EDGE,{"disambiguationData":[TD([[subQ2,1.0]])],"derivedFrom":subQ1}),1.0]])]});}
            var Q20;
            {var subQ0=sQuery(id+"F9.wireOp",EDGE,"E22.8.0.1");var subQ1=sQuery(id+"F9.wireOp",EDGE,"E12.top");var subQ2=makeQuery(id+"F9.imprint","INTERSECT",VERTEX,{"derivedFrom":[subQ1,subQ0]});Q20=makeQuery(id+"F9.imprint","IMPRINT",FACE,{"disambiguationData":[TD([[makeQuery(id+"F9.imprint","IMPRINT",EDGE,{"disambiguationData":[TD([[subQ2,1.0]])],"derivedFrom":subQ1}),1.0]])]});}
            var Q21;
            {var subQ0=sQuery(id+"F9.wireOp",EDGE,"E22.8.0.3");var subQ1=sQuery(id+"F9.wireOp",EDGE,"E12.bottom");var subQ2=makeQuery(id+"F9.imprint","INTERSECT",VERTEX,{"derivedFrom":[subQ1,subQ0]});Q21=makeQuery(id+"F9.imprint","IMPRINT",FACE,{"disambiguationData":[TD([[makeQuery(id+"F9.imprint","IMPRINT",EDGE,{"disambiguationData":[TD([[subQ2,1.0]])],"derivedFrom":subQ1}),-1.0]])]});}
            var Q22;
            {var subQ0=sQuery(id+"F9.wireOp",EDGE,"E22.7.0.3");var subQ1=sQuery(id+"F9.wireOp",EDGE,"E12.bottom");var subQ2=makeQuery(id+"F9.imprint","INTERSECT",VERTEX,{"derivedFrom":[subQ1,subQ0]});Q22=makeQuery(id+"F9.imprint","IMPRINT",FACE,{"disambiguationData":[TD([[makeQuery(id+"F9.imprint","IMPRINT",EDGE,{"disambiguationData":[TD([[subQ2,1.0]])],"derivedFrom":subQ1}),-1.0]])]});}
            var Q23;
            {var subQ0=sQuery(id+"F9.wireOp",EDGE,"E22.7.0.1");var subQ1=sQuery(id+"F9.wireOp",EDGE,"E12.top");var subQ2=makeQuery(id+"F9.imprint","INTERSECT",VERTEX,{"derivedFrom":[subQ1,subQ0]});Q23=makeQuery(id+"F9.imprint","IMPRINT",FACE,{"disambiguationData":[TD([[makeQuery(id+"F9.imprint","IMPRINT",EDGE,{"disambiguationData":[TD([[subQ2,1.0]])],"derivedFrom":subQ1}),1.0]])]});}
            var Q24;
            {var subQ0=sQuery(id+"F9.wireOp",EDGE,"E22.6.0.1");var subQ1=sQuery(id+"F9.wireOp",EDGE,"E12.top");var subQ2=makeQuery(id+"F9.imprint","INTERSECT",VERTEX,{"derivedFrom":[subQ1,subQ0]});Q24=makeQuery(id+"F9.imprint","IMPRINT",FACE,{"disambiguationData":[TD([[makeQuery(id+"F9.imprint","IMPRINT",EDGE,{"disambiguationData":[TD([[subQ2,1.0]])],"derivedFrom":subQ1}),1.0]])]});}
            var Q25;
            {var subQ0=sQuery(id+"F9.wireOp",EDGE,"E22.6.0.3");var subQ1=sQuery(id+"F9.wireOp",EDGE,"E12.bottom");var subQ2=makeQuery(id+"F9.imprint","INTERSECT",VERTEX,{"derivedFrom":[subQ1,subQ0]});Q25=makeQuery(id+"F9.imprint","IMPRINT",FACE,{"disambiguationData":[TD([[makeQuery(id+"F9.imprint","IMPRINT",EDGE,{"disambiguationData":[TD([[subQ2,1.0]])],"derivedFrom":subQ1}),-1.0]])]});}
            var Q26;
            {var subQ0=sQuery(id+"F9.wireOp",EDGE,"E22.5.0.3");var subQ1=sQuery(id+"F9.wireOp",EDGE,"E12.bottom");var subQ2=makeQuery(id+"F9.imprint","INTERSECT",VERTEX,{"derivedFrom":[subQ1,subQ0]});Q26=makeQuery(id+"F9.imprint","IMPRINT",FACE,{"disambiguationData":[TD([[makeQuery(id+"F9.imprint","IMPRINT",EDGE,{"disambiguationData":[TD([[subQ2,1.0]])],"derivedFrom":subQ1}),-1.0]])]});}
            var Q27;
            {var subQ0=sQuery(id+"F9.wireOp",EDGE,"E22.5.0.1");var subQ1=sQuery(id+"F9.wireOp",EDGE,"E12.top");var subQ2=makeQuery(id+"F9.imprint","INTERSECT",VERTEX,{"derivedFrom":[subQ1,subQ0]});Q27=makeQuery(id+"F9.imprint","IMPRINT",FACE,{"disambiguationData":[TD([[makeQuery(id+"F9.imprint","IMPRINT",EDGE,{"disambiguationData":[TD([[subQ2,1.0]])],"derivedFrom":subQ1}),1.0]])]});}
            var Q28;
            {var subQ0=sQuery(id+"F9.wireOp",EDGE,"E22.9.0.3");var subQ1=sQuery(id+"F9.wireOp",EDGE,"E12.bottom");var subQ2=makeQuery(id+"F9.imprint","INTERSECT",VERTEX,{"derivedFrom":[subQ1,subQ0]});Q28=makeQuery(id+"F9.imprint","IMPRINT",FACE,{"disambiguationData":[TD([[makeQuery(id+"F9.imprint","IMPRINT",EDGE,{"disambiguationData":[TD([[subQ2,1.0]])],"derivedFrom":subQ1}),-1.0]])]});}
            var Q29;
            {var subQ0=sQuery(id+"F9.wireOp",EDGE,"E22.4.0.3");var subQ1=sQuery(id+"F9.wireOp",EDGE,"E12.bottom");var subQ2=makeQuery(id+"F9.imprint","INTERSECT",VERTEX,{"derivedFrom":[subQ1,subQ0]});Q29=makeQuery(id+"F9.imprint","IMPRINT",FACE,{"disambiguationData":[TD([[makeQuery(id+"F9.imprint","IMPRINT",EDGE,{"disambiguationData":[TD([[subQ2,1.0]])],"derivedFrom":subQ1}),-1.0]])]});}
            var Q30;
            {var subQ0=sQuery(id+"F9.wireOp",EDGE,"E22.4.0.1");var subQ1=sQuery(id+"F9.wireOp",EDGE,"E12.top");var subQ2=makeQuery(id+"F9.imprint","INTERSECT",VERTEX,{"derivedFrom":[subQ1,subQ0]});Q30=makeQuery(id+"F9.imprint","IMPRINT",FACE,{"disambiguationData":[TD([[makeQuery(id+"F9.imprint","IMPRINT",EDGE,{"disambiguationData":[TD([[subQ2,1.0]])],"derivedFrom":subQ1}),1.0]])]});}
            var Q31;
            {var subQ0=sQuery(id+"F9.wireOp",EDGE,"E22.3.0.1");var subQ1=sQuery(id+"F9.wireOp",EDGE,"E12.top");var subQ2=makeQuery(id+"F9.imprint","INTERSECT",VERTEX,{"derivedFrom":[subQ1,subQ0]});Q31=makeQuery(id+"F9.imprint","IMPRINT",FACE,{"disambiguationData":[TD([[makeQuery(id+"F9.imprint","IMPRINT",EDGE,{"disambiguationData":[TD([[subQ2,1.0]])],"derivedFrom":subQ1}),1.0]])]});}
            var Q32;
            {var subQ0=sQuery(id+"F9.wireOp",EDGE,"E22.3.0.3");var subQ1=sQuery(id+"F9.wireOp",EDGE,"E12.bottom");var subQ2=makeQuery(id+"F9.imprint","INTERSECT",VERTEX,{"derivedFrom":[subQ1,subQ0]});Q32=makeQuery(id+"F9.imprint","IMPRINT",FACE,{"disambiguationData":[TD([[makeQuery(id+"F9.imprint","IMPRINT",EDGE,{"disambiguationData":[TD([[subQ2,1.0]])],"derivedFrom":subQ1}),-1.0]])]});}
            var Q33;
            {var subQ0=sQuery(id+"F9.wireOp",EDGE,"E22.2.0.3");var subQ1=sQuery(id+"F9.wireOp",EDGE,"E12.bottom");var subQ2=makeQuery(id+"F9.imprint","INTERSECT",VERTEX,{"derivedFrom":[subQ1,subQ0]});Q33=makeQuery(id+"F9.imprint","IMPRINT",FACE,{"disambiguationData":[TD([[makeQuery(id+"F9.imprint","IMPRINT",EDGE,{"disambiguationData":[TD([[subQ2,1.0]])],"derivedFrom":subQ1}),-1.0]])]});}
            var Q34;
            {var subQ0=sQuery(id+"F9.wireOp",EDGE,"E22.2.0.1");var subQ1=sQuery(id+"F9.wireOp",EDGE,"E12.top");var subQ2=makeQuery(id+"F9.imprint","INTERSECT",VERTEX,{"derivedFrom":[subQ1,subQ0]});Q34=makeQuery(id+"F9.imprint","IMPRINT",FACE,{"disambiguationData":[TD([[makeQuery(id+"F9.imprint","IMPRINT",EDGE,{"disambiguationData":[TD([[subQ2,1.0]])],"derivedFrom":subQ1}),1.0]])]});}
            var Q35;
            {var subQ0=sQuery(id+"F9.wireOp",EDGE,"E22.1.0.1");var subQ1=sQuery(id+"F9.wireOp",EDGE,"E12.top");var subQ2=makeQuery(id+"F9.imprint","INTERSECT",VERTEX,{"derivedFrom":[subQ1,subQ0]});Q35=makeQuery(id+"F9.imprint","IMPRINT",FACE,{"disambiguationData":[TD([[makeQuery(id+"F9.imprint","IMPRINT",EDGE,{"disambiguationData":[TD([[subQ2,1.0]])],"derivedFrom":subQ1}),1.0]])]});}
            var Q36;
            {var subQ0=sQuery(id+"F9.wireOp",EDGE,"E22.1.0.3");var subQ1=sQuery(id+"F9.wireOp",EDGE,"E12.bottom");var subQ2=makeQuery(id+"F9.imprint","INTERSECT",VERTEX,{"derivedFrom":[subQ1,subQ0]});Q36=makeQuery(id+"F9.imprint","IMPRINT",FACE,{"disambiguationData":[TD([[makeQuery(id+"F9.imprint","IMPRINT",EDGE,{"disambiguationData":[TD([[subQ2,1.0]])],"derivedFrom":subQ1}),-1.0]])]});}
            var Q37;
            {var subQ0=sQuery(id+"F9.wireOp",EDGE,"E21.MirrorCS");var subQ1=sQuery(id+"F9.wireOp",EDGE,"E12.bottom");var subQ2=makeQuery(id+"F9.imprint","INTERSECT",VERTEX,{"derivedFrom":[subQ1,subQ0]});Q37=makeQuery(id+"F9.imprint","IMPRINT",FACE,{"disambiguationData":[TD([[makeQuery(id+"F9.imprint","IMPRINT",EDGE,{"disambiguationData":[TD([[subQ2,1.0]])],"derivedFrom":subQ1}),-1.0]])]});}
            var Q38;
            {var subQ1=sQuery(id+"F9.wireOp",EDGE,"E12.top");var subQ3=sQuery(id+"F9.wireOp",EDGE,"E19");var subQ4=makeQuery(id+"F9.imprint","INTERSECT",VERTEX,{"derivedFrom":[subQ1,subQ3]});Q38=makeQuery(id+"F9.imprint","IMPRINT",FACE,{"disambiguationData":[TD([[makeQuery(id+"F9.imprint","IMPRINT",EDGE,{"disambiguationData":[TD([[subQ4,1.0]])],"derivedFrom":subQ3}),1.0]])]});}
            var Q39;
            {var subQ1=sQuery(id+"F9.wireOp",EDGE,"E12.bottom");var subQ3=sQuery(id+"F9.wireOp",EDGE,"E20.MirrorCS");var subQ4=makeQuery(id+"F9.imprint","INTERSECT",VERTEX,{"derivedFrom":[subQ1,subQ3]});Q39=makeQuery(id+"F9.imprint","IMPRINT",FACE,{"disambiguationData":[TD([[makeQuery(id+"F9.imprint","IMPRINT",EDGE,{"disambiguationData":[TD([[subQ4,1.0]])],"derivedFrom":subQ3}),-1.0]])]});}
            var Q40;
            {var subQ1=sQuery(id+"F9.wireOp",EDGE,"E13");var subQ3=sQuery(id+"F9.wireOp",EDGE,"E19");var subQ4=makeQuery(id+"F9.imprint","INTERSECT",VERTEX,{"derivedFrom":[subQ1,subQ3]});Q40=makeQuery(id+"F9.imprint","IMPRINT",FACE,{"disambiguationData":[TD([[makeQuery(id+"F9.imprint","IMPRINT",EDGE,{"disambiguationData":[TD([[subQ4,-1.0]])],"derivedFrom":subQ3}),1.0]])]});}
            var Q41;
            {var subQ0=sQuery(id+"F9.wireOp",EDGE,"E18");var subQ1=sQuery(id+"F9.wireOp",EDGE,"E12.top");var subQ2=makeQuery(id+"F9.imprint","INTERSECT",VERTEX,{"derivedFrom":[subQ1,subQ0]});Q41=makeQuery(id+"F9.imprint","IMPRINT",FACE,{"disambiguationData":[TD([[makeQuery(id+"F9.imprint","IMPRINT",EDGE,{"disambiguationData":[TD([[subQ2,1.0]])],"derivedFrom":subQ1}),1.0]])]});}
            extrude(context, id + "F10", {"entities" : qUnion([Q0, Q1, Q2, Q3, Q4, Q5, Q6, Q7, Q8, Q9, Q10, Q11, Q12, Q13, Q14, Q15, Q16, Q17, Q18, Q19, Q20, Q21, Q22, Q23, Q24, Q25, Q26, Q27, Q28, Q29, Q30, Q31, Q32, Q33, Q34, Q35, Q36, Q37, Q38, Q39, Q40, Q41]), "operationType" : NewBodyOperationType.REMOVE, "endBound" : BoundingType.SYMMETRIC, "oppositeDirection" : true, "depth" : (getVariable(context, 'Width')) * mm, "offsetDistance" : 25 * mm});
        }
    });
